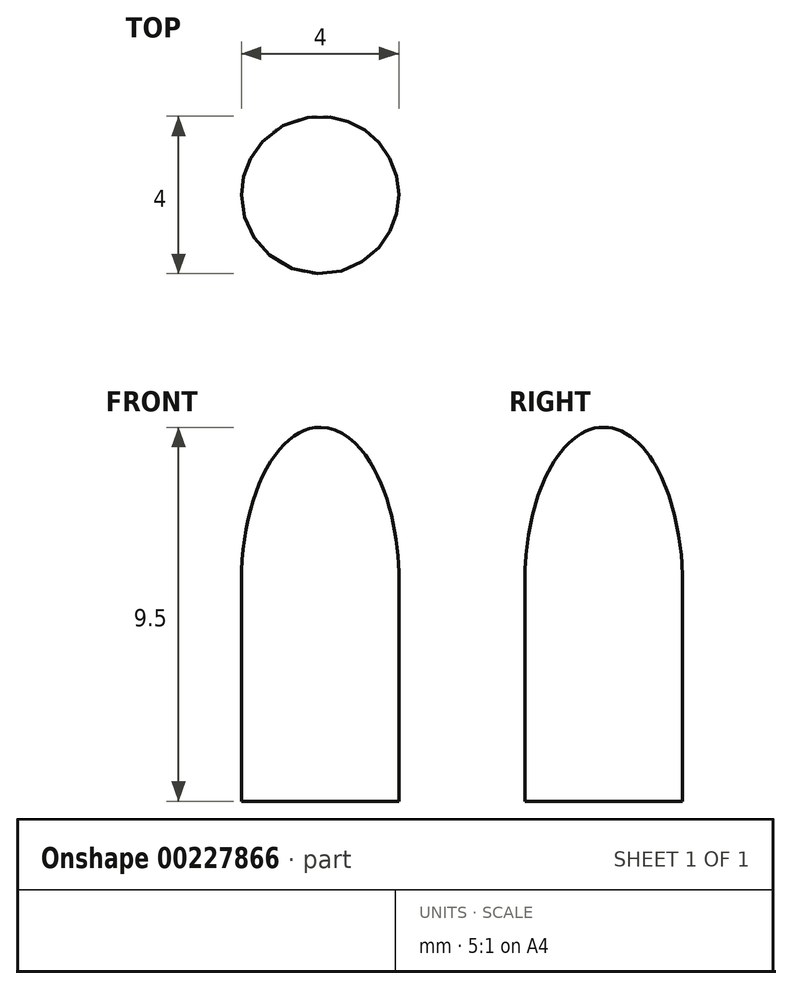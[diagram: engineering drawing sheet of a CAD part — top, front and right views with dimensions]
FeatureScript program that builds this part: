
annotation { "Feature Type Name" : "Feature", "Feature Type Description" : "" }
export const myFeature = defineFeature(function(context is Context, id is Id, definition is map)
    precondition{}
    {
        {
            var Q0;
            Q0=qCreatedBy(makeId("Front.planeOp"),FACE);
            var sketch = newSketch(context, id + "F0", { "sketchPlane" : qUnion([Q0])});
            skLineSegment(sketch, "E0", {"start": v(0, 0) * mm, "end": v(0, 5.6) * mm, "construction": true});
            skPoint(sketch, "E1.visualSharp", {"position": v(-2, 5.6) * mm});
            skLineSegment(sketch, "E2", {"start": v(0, 5.6) * mm, "end": v(0, 9.5) * mm, "construction": true});
            skEllipticalArc(sketch, "E3", {});
            skLineSegment(sketch, "E4", {"start": v(0, 0) * mm, "end": v(-2, 0) * mm});
            skLineSegment(sketch, "E5", {"start": v(-2, 0) * mm, "end": v(-2, 5.6) * mm});
            skLineSegment(sketch, "E6", {"start": v(0, 0) * mm, "end": v(0, 9.5) * mm});
            const initialGuessF0  = {"E3": [0, 0.0056, 0, 1, 0.0039, 0.002, 0, 1.5707963267948966]};
            skSetInitialGuess(sketch, initialGuessF0);
            skSolve(sketch);
        }
        {
            var Q0;
            Q0=qSketchRegion(id+"F0",true);
            var Q1;
            Q1=sQuery(id+"F0.wireOp",EDGE,"E6");
            revolve(context, id + "F1", {"entities" : qUnion([Q0]), "axis" : qUnion([Q1]), "revolveType" : RevolveType.FULL});
        }
    });
